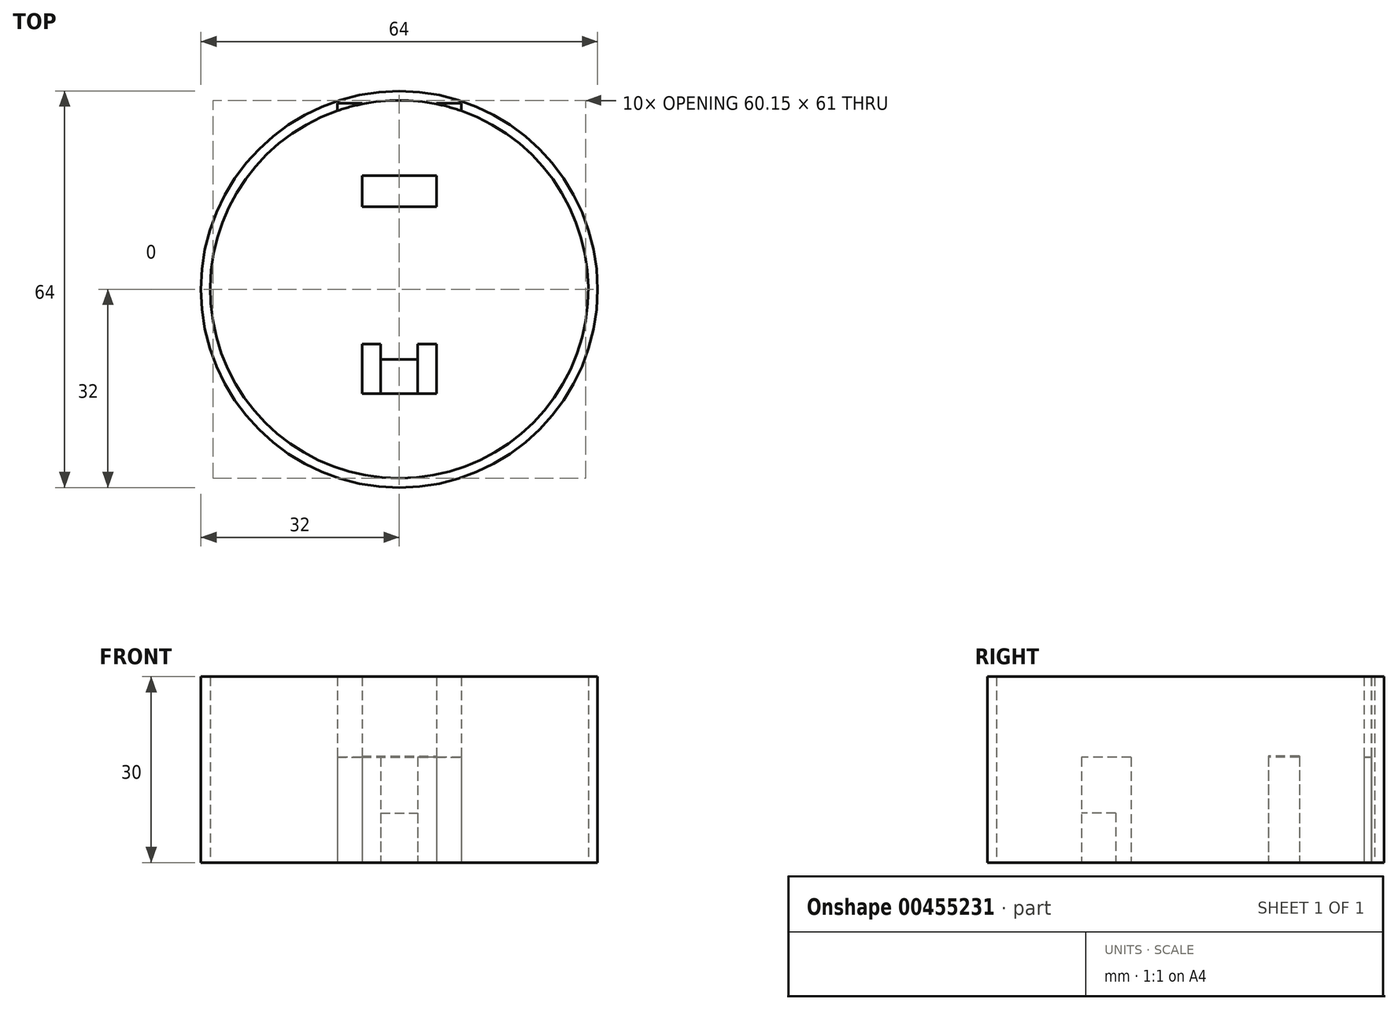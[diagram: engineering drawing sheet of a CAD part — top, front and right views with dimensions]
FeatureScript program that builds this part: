
annotation { "Feature Type Name" : "Feature", "Feature Type Description" : "" }
export const myFeature = defineFeature(function(context is Context, id is Id, definition is map)
    precondition{}
    {
        {
            var Q0;
            Q0=qCreatedBy(makeId("Top.planeOp"),FACE);
            var sketch = newSketch(context, id + "F0", { "sketchPlane" : qUnion([Q0])});
            skLineSegment(sketch, "E0.bottom", {"start": v(-10, 30) * mm, "end": v(-6, 30) * mm});
            skLineSegment(sketch, "E0.top", {"start": v(-10, -30) * mm, "end": v(-6, -30) * mm});
            skLineSegment(sketch, "E0.left", {"start": v(-10, 30) * mm, "end": v(-10, -30) * mm});
            skLineSegment(sketch, "E0.right", {"start": v(-6, 30) * mm, "end": v(-6, -30) * mm});
            skLineSegment(sketch, "E1.bottom", {"start": v(-6, 18.35) * mm, "end": v(6, 18.35) * mm});
            skLineSegment(sketch, "E1.top", {"start": v(-6, 13.35) * mm, "end": v(6, 13.35) * mm});
            skLineSegment(sketch, "E1.left", {"start": v(-6, 18.35) * mm, "end": v(-6, 13.35) * mm});
            skLineSegment(sketch, "E1.right", {"start": v(6, 18.35) * mm, "end": v(6, 13.35) * mm});
            skLineSegment(sketch, "E2.bottom", {"start": v(6, 30) * mm, "end": v(10, 30) * mm});
            skLineSegment(sketch, "E2.top", {"start": v(6, -30) * mm, "end": v(10, -30) * mm});
            skLineSegment(sketch, "E2.left", {"start": v(6, 30) * mm, "end": v(6, -30) * mm});
            skLineSegment(sketch, "E2.right", {"start": v(10, 30) * mm, "end": v(10, -30) * mm});
            skLineSegment(sketch, "E3.bottom", {"start": v(-6, -8.8) * mm, "end": v(-3, -8.8) * mm});
            skLineSegment(sketch, "E3.top", {"start": v(-6, -16.8) * mm, "end": v(-3, -16.8) * mm});
            skLineSegment(sketch, "E3.left", {"start": v(-6, -8.8) * mm, "end": v(-6, -16.8) * mm});
            skLineSegment(sketch, "E3.right", {"start": v(-3, -8.8) * mm, "end": v(-3, -16.8) * mm});
            skLineSegment(sketch, "E4.bottom", {"start": v(6, -8.8) * mm, "end": v(3, -8.8) * mm});
            skLineSegment(sketch, "E4.top", {"start": v(6, -16.8) * mm, "end": v(3, -16.8) * mm});
            skLineSegment(sketch, "E4.left", {"start": v(6, -8.8) * mm, "end": v(6, -16.8) * mm});
            skLineSegment(sketch, "E4.right", {"start": v(3, -8.8) * mm, "end": v(3, -16.8) * mm});
            skLineSegment(sketch, "E5", {"start": v(-3, -16.8) * mm, "end": v(3, -16.8) * mm});
            skLineSegment(sketch, "E6", {"start": v(-3, -11.28) * mm, "end": v(3, -11.28) * mm});
            skLineSegment(sketch, "E7", {"start": v(6, 0) * mm, "end": v(-6, 0) * mm});
            skPoint(sketch, "E8", {"position": v(0, 0) * mm});
            skCircle(sketch, "E9", {"center": v(0, 0) * mm, "radius": 30.5 * mm});
            skCircle(sketch, "E10", {"center": v(0, 0) * mm, "radius": 32 * mm});
            skSolve(sketch);
        }
        {
            var Q0;
            {var subQ4=sQuery(id+"F0.wireOp",EDGE,"E2.bottom");Q0=makeQuery(id+"F0.imprint","IMPRINT",FACE,{"disambiguationData":[TD([[makeQuery(id+"F0.imprint","IMPRINT",EDGE,{"derivedFrom":subQ4}),-1.0]])]});}
            var Q1;
            {var subQ0=sQuery(id+"F0.wireOp",EDGE,"E1.bottom");Q1=makeQuery(id+"F0.imprint","IMPRINT",FACE,{"disambiguationData":[TD([[makeQuery(id+"F0.imprint","IMPRINT",EDGE,{"derivedFrom":subQ0}),-1.0]])]});}
            var Q2;
            {var subQ1=sQuery(id+"F0.wireOp",EDGE,"E0.bottom");Q2=makeQuery(id+"F0.imprint","IMPRINT",FACE,{"disambiguationData":[TD([[makeQuery(id+"F0.imprint","IMPRINT",EDGE,{"derivedFrom":subQ1}),-1.0]])]});}
            var Q3;
            {var subQ1=sQuery(id+"F0.wireOp",EDGE,"E3.bottom");Q3=makeQuery(id+"F0.imprint","IMPRINT",FACE,{"disambiguationData":[TD([[makeQuery(id+"F0.imprint","IMPRINT",EDGE,{"derivedFrom":subQ1}),-1.0]])]});}
            var Q4;
            {var subQ1=sQuery(id+"F0.wireOp",EDGE,"E4.bottom");Q4=makeQuery(id+"F0.imprint","IMPRINT",FACE,{"disambiguationData":[TD([[makeQuery(id+"F0.imprint","IMPRINT",EDGE,{"derivedFrom":subQ1}),1.0]])]});}
            extrude(context, id + "F1", {"entities" : qUnion([Q0, Q1, Q2, Q3, Q4]), "depth" : 17 * mm});
        }
        {
            var Q0;
            {var subQ0=sQuery(id+"F0.wireOp",EDGE,"E5");Q0=makeQuery(id+"F0.imprint","IMPRINT",FACE,{"disambiguationData":[TD([[makeQuery(id+"F0.imprint","IMPRINT",EDGE,{"derivedFrom":subQ0}),1.0]])]});}
            extrude(context, id + "F2", {"entities" : qUnion([Q0]), "operationType" : NewBodyOperationType.ADD, "depth" : 8 * mm});
        }
        {
            var Q0;
            Q0 = qSketchRegion(id + "F0", true);
            var Q1;
            {var subQ0=sQuery(id+"F0.wireOp",EDGE,"E0.top");Q1=makeQuery(id+"F0.imprint","IMPRINT",FACE,{"disambiguationData":[TD([[makeQuery(id+"F0.imprint","IMPRINT",EDGE,{"derivedFrom":subQ0}),1.0]])]});}
            var Q2;
            {var subQ0=sQuery(id+"F0.wireOp",EDGE,"E2.top");Q2=makeQuery(id+"F0.imprint","IMPRINT",FACE,{"disambiguationData":[TD([[makeQuery(id+"F0.imprint","IMPRINT",EDGE,{"derivedFrom":subQ0}),1.0]])]});}
            extrude(context, id + "F3", {"entities" : qUnion([Q0, Q1, Q2]), "depth" : 30 * mm});
        }
        {
            var Q0;
            {var subQ0=sQuery(id+"F0.wireOp",EDGE,"E4.left");Q0=makeQuery(id+"F0.imprint","IMPRINT",FACE,{"disambiguationData":[TD([[makeQuery(id+"F0.imprint","IMPRINT",EDGE,{"derivedFrom":subQ0}),1.0]])]});}
            var Q1;
            {var subQ0=sQuery(id+"F0.wireOp",EDGE,"E1.left");Q1=makeQuery(id+"F0.imprint","IMPRINT",FACE,{"disambiguationData":[TD([[makeQuery(id+"F0.imprint","IMPRINT",EDGE,{"derivedFrom":subQ0}),-1.0]])]});}
            var Q2;
            {var subQ0=sQuery(id+"F0.wireOp",EDGE,"E1.bottom");Q2=makeQuery(id+"F0.imprint","IMPRINT",FACE,{"disambiguationData":[TD([[makeQuery(id+"F0.imprint","IMPRINT",EDGE,{"derivedFrom":subQ0}),-1.0]])]});}
            extrude(context, id + "F4", {"entities" : qUnion([Q0, Q1, Q2]), "depth" : 17.2 * mm});
        }
    });
